# Revit family: FI_2014
name_source: partatom
category: Specialty Equipment
revit_build: Autodesk Revit 2014 (Build: 20130308_1515(x64)
units: mm (PartAtom-declared; Revit-internal decimal feet)

## types (2) — shared parameters
Bumper = Extruded PVC - 701 Black
Case = Textured Sheet Metal (Steel Painted) - 149 White Satin Matte
Close Off Panel = Textured Sheet Metal (Steel Painted) - 701 Black
Cutsheet URL = http://www.hussmann.com
Depth = 58"
Description = Intermediate Island for Frozen Food
End Weight = 50.00 lbf
Ends = Textured Sheet Metal (Steel Painted) - 149 White Satin Matte
Glazing = Glass
Height = 35 7/8"
Manufacturer = Hussmann Corporation
Manufacturer Disclaimer = The information in this file is not intended to be an exact representation of the corresponding Hussmann product.  Further, we reserve the right to change or revise specifications and product design in connection with any feature of our products. Such changes do not entitle the buyer to corresponding changes, improvements, additions, or replacements for equipment previously sold or shipped.
Model = FI
Model URL = http://www.hussmann.com
Note from Manufacturer = This model only comes in 8'-0" and 12'-0" lengths.
Refrig. Liquid = Liquid
Refrig. Suction = Suction
Refrigeration Lines Liquid = 3/8"
Refrigeration Lines Suction = 5/8"
Revit Family Date = 08/30/2016
Shelves = Sheet Metal (Steel Painted) - 700 Interior White
Splashguard = Textured Sheet Metal (Steel Painted) - 701 Black
Type Comments = Excel
URL = www.hussmann.com
Waste Drain = 1 1/4"

## per-type parameters (varying)
| type | Case Interior - Back Panel | Case Interior - Side Panel | Case Weight | Number of Supports | Total Weight | Trim | Width |
| 12'-0" Length | Mirror | Mirror | 1200.00 lbf | 4 | 1300.00 lbf | Stainless Steel | 144 1/2" |
| 8'-0" Length | Sheet Metal (Steel Painted) - 700 Interior White | Sheet Metal (Steel Painted) - 700 Interior White | 1000.00 lbf | 3 | 1100.00 lbf | Plastic - 144 Mist Gray | 96 3/8" |

## geometry (parser evidence)
native form markers: Sweep x10
no freeform markers — native parametric forms only
